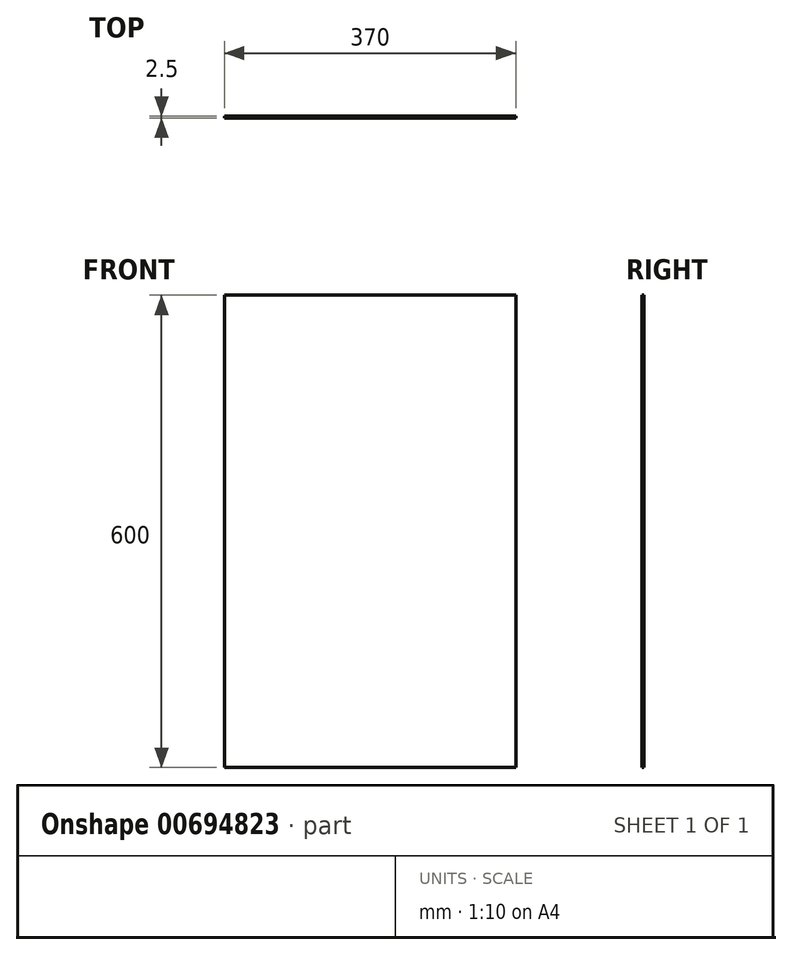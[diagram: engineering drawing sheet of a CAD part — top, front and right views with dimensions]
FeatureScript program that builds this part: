
annotation { "Feature Type Name" : "Feature", "Feature Type Description" : "" }
export const myFeature = defineFeature(function(context is Context, id is Id, definition is map)
    precondition{}
    {
        {
            var Q0;
            Q0=qCreatedBy(makeId("Front.planeOp"),FACE);
            var sketch = newSketch(context, id + "F0", { "sketchPlane" : qUnion([Q0])});
            skLineSegment(sketch, "E0.bottom", {"start": v(0, 0) * mm, "end": v(370, 0) * mm});
            skLineSegment(sketch, "E0.top", {"start": v(0, 600) * mm, "end": v(370, 600) * mm});
            skLineSegment(sketch, "E0.left", {"start": v(0, 0) * mm, "end": v(0, 600) * mm});
            skLineSegment(sketch, "E0.right", {"start": v(370, 0) * mm, "end": v(370, 600) * mm});
            skSolve(sketch);
        }
        {
            var Q0;
            Q0 = qSketchRegion(id + "F0", true);
            extrude(context, id + "F1", {"entities" : qUnion([Q0]), "depth" : 2.5 * mm, "offsetDistance" : 25 * mm});
        }
    });
